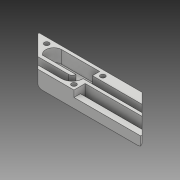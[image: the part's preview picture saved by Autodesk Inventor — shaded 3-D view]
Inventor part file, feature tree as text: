
AUTODESK INVENTOR PART (.ipt)
format: ipt  version: 2018 (Build 220112000, 112)  size: 209,920 bytes
history: native  units: mm
features: sketch x8, extrude x6, other x2, fillet x2, projected_geometry x2, shell x1, sweep x1, chamfer x1
ambient origin geometry x8: Origin, YZ Plane, XZ Plane, XY Plane, X Axis, Y Axis, Z Axis, Center Point
bodies: Body1 (feature_tree)
feature tree (23):
  other  "ソリッド1"
  extrude  "押し出し1"  TaperAngle=45.0deg  [1 undecoded]
  extrude  "押し出し3"  Depth=20.0mm
  extrude  "押し出し4"  Depth=65.0mm
  shell  "シェル1"  Thickness=20.0mm
  fillet  "フィレット2"  Radius=15.5mm
  sketch  "スケッチ7"
  extrude  "押し出し6"  Depth=3.0mm
  other  "作業平面1"
  sweep  "スイープ1"
  extrude  "押し出し7"  Depth=3.75mm
  extrude  "押し出し8"  Depth=3.75mm
  chamfer  "面取り1"  Distance=35.0mm
  fillet  "フィレット4"  Radius=10.0mm
  sketch  "スケッチ1"
  sketch  "スケッチ3"
  sketch  "スケッチ4"
  sketch  "スケッチ6"
  projected_geometry  "投影ループ1"
  sketch  "スケッチ8"
  sketch  "スケッチ9"
  sketch  "スケッチ10"
  projected_geometry  "投影ループ2"
note: 1 required parameter value undecoded (feature->parameter linkage not recoverable at this tier; creation-order binding heuristic only, values carry confidence <= 0.55)
